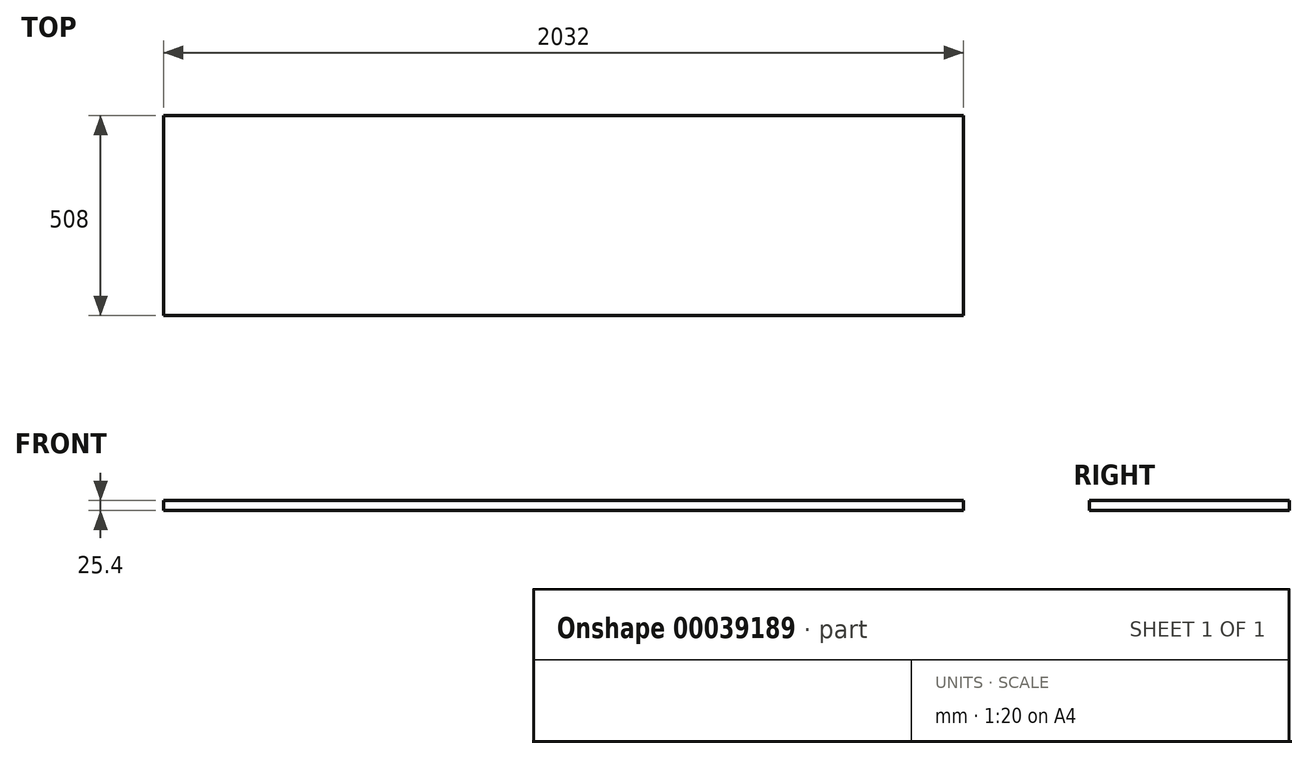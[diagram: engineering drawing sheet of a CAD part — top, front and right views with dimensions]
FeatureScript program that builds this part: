
annotation { "Feature Type Name" : "Feature", "Feature Type Description" : "" }
export const myFeature = defineFeature(function(context is Context, id is Id, definition is map)
    precondition{}
    {
        {
            var Q0;
            Q0=qCreatedBy(makeId("Top.planeOp"),FACE);
            var sketch = newSketch(context, id + "F0", { "sketchPlane" : qUnion([Q0])});
            skLineSegment(sketch, "E0.bottom", {"start": v(-1018.26, -63.44) * mm, "end": v(1013.74, -63.44) * mm});
            skLineSegment(sketch, "E0.top", {"start": v(-1018.26, -571.44) * mm, "end": v(1013.74, -571.44) * mm});
            skLineSegment(sketch, "E0.left", {"start": v(-1018.26, -63.44) * mm, "end": v(-1018.26, -571.44) * mm});
            skLineSegment(sketch, "E0.right", {"start": v(1013.74, -63.44) * mm, "end": v(1013.74, -571.44) * mm});
            skSolve(sketch);
        }
        {
            var Q0;
            Q0=makeQuery(id+"F0.imprint","IMPRINT",FACE,{"disambiguationData":[TD([[makeQuery(id+"F0.imprint","IMPRINT",EDGE,{"derivedFrom":sQuery(id+"F0.wireOp",EDGE,"E0.bottom")}),-1.0]])]});
            extrude(context, id + "F1", {"entities" : qUnion([Q0]), "depth" : 25.4 * mm});
        }
    });
